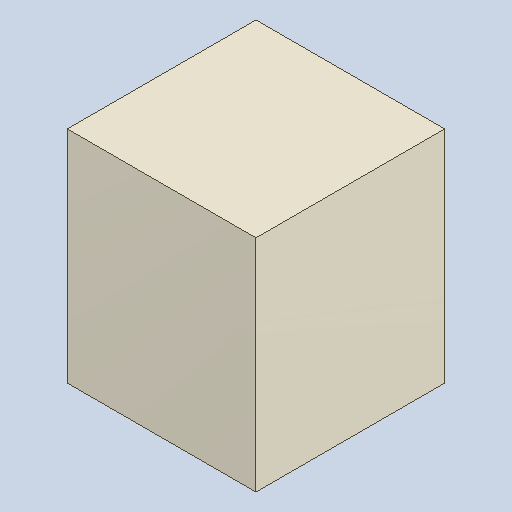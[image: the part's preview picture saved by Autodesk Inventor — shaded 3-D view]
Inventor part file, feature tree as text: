
AUTODESK INVENTOR PART (.ipt)
format: ipt  version: 2023.4 (Build 274418000, 418)  size: 82,944 bytes
history: native  units: mm
features: extrude x1
ambient origin geometry x8: Origin, YZ Plane, XZ Plane, XY Plane, X Axis, Y Axis, Z Axis, Center Point
bodies: Solid1 (feature_tree)
feature tree (1):
  extrude  "Extruded_10"  [1 undecoded]
note: 1 required parameter value undecoded (feature->parameter linkage not recoverable at this tier; creation-order binding heuristic only, values carry confidence <= 0.55)
